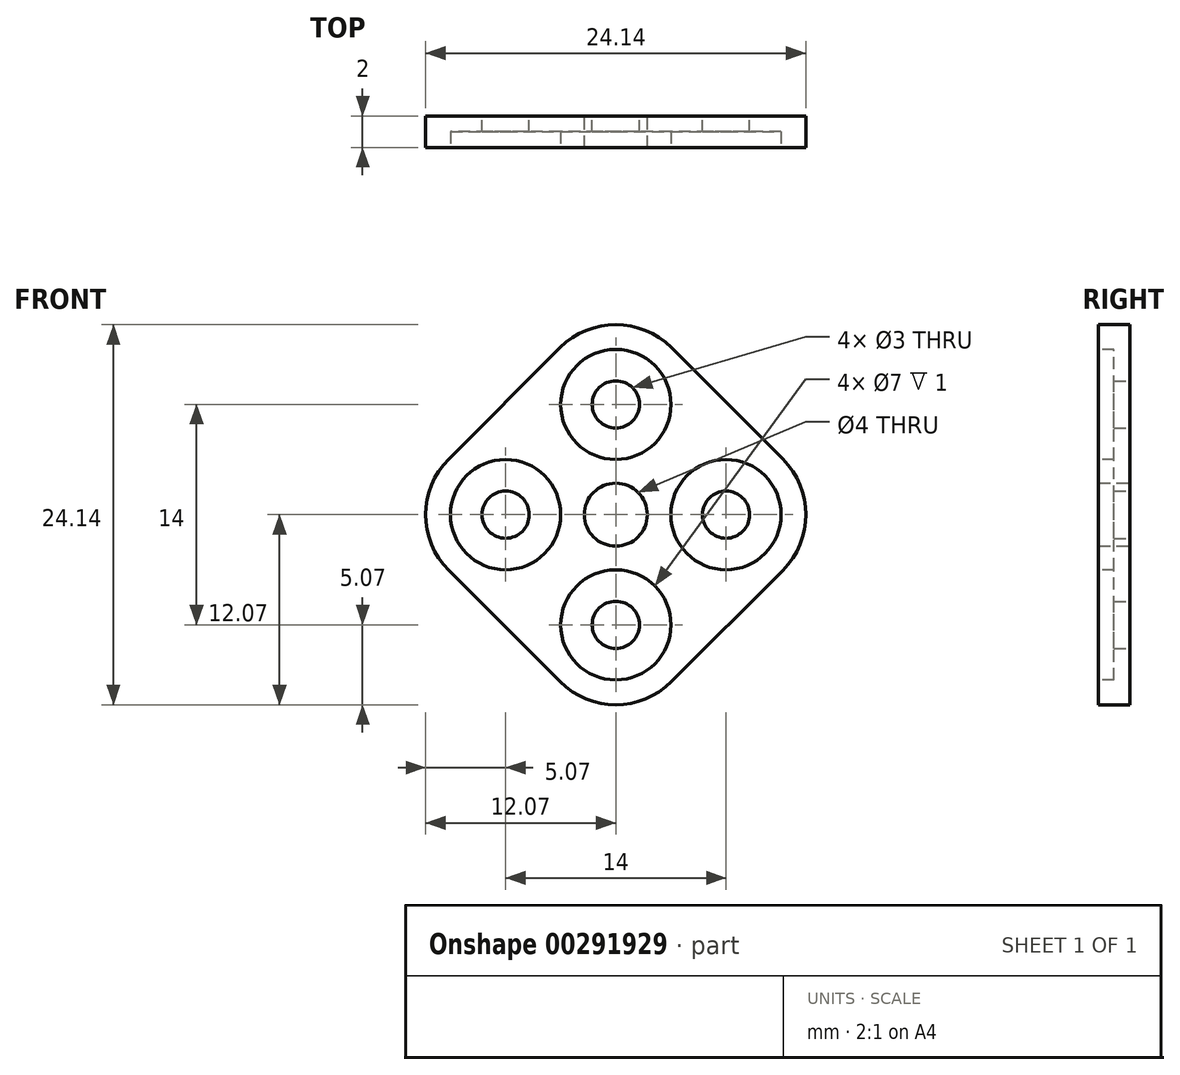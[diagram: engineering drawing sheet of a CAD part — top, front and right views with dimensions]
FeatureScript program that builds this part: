
annotation { "Feature Type Name" : "Feature", "Feature Type Description" : "" }
export const myFeature = defineFeature(function(context is Context, id is Id, definition is map)
    precondition{}
    {
        {
            var Q0;
            Q0=qCreatedBy(makeId("Front.planeOp"),FACE);
            var sketch = newSketch(context, id + "F0", { "sketchPlane" : qUnion([Q0])});
            skPoint(sketch, "E0.middle", {"position": v(0, 0) * mm});
            skCircle(sketch, "E1", {"center": v(0, 0) * mm, "radius": 2 * mm});
            skCircle(sketch, "E2", {"center": v(7, 0) * mm, "radius": 1.5 * mm});
            skCircle(sketch, "E3.1.0", {"center": v(0, 7) * mm, "radius": 1.5 * mm});
            skCircle(sketch, "E3.2.0", {"center": v(-7, 0) * mm, "radius": 1.5 * mm});
            skCircle(sketch, "E3.3.0", {"center": v(0, -7) * mm, "radius": 1.5 * mm});
            skPoint(sketch, "E4.endSnap0", {"position": v(0, -11.8) * mm});
            skLineSegment(sketch, "E5.bottom", {"start": v(-3.54, -10.6) * mm, "end": v(-10.6, -3.54) * mm});
            skLineSegment(sketch, "E5.top", {"start": v(10.6, 3.54) * mm, "end": v(3.54, 10.6) * mm});
            skLineSegment(sketch, "E5.left", {"start": v(3.54, -10.6) * mm, "end": v(10.6, -3.54) * mm});
            skLineSegment(sketch, "E5.right", {"start": v(-10.6, 3.54) * mm, "end": v(-3.54, 10.6) * mm});
            skPoint(sketch, "E6.visualSharp", {"position": v(0, -14.14) * mm});
            skArc(sketch, "E6.filletArc", {"start": v(-3.54, -10.6) * mm, "mid": v(0, -12.07) * mm, "end": v(3.54, -10.6) * mm});
            skPoint(sketch, "E7.visualSharp", {"position": v(-14.14, 0) * mm});
            skArc(sketch, "E7.filletArc", {"start": v(-10.6, 3.54) * mm, "mid": v(-12.07, 0) * mm, "end": v(-10.6, -3.54) * mm});
            skPoint(sketch, "E8.visualSharp", {"position": v(0, 14.14) * mm});
            skArc(sketch, "E8.filletArc", {"start": v(3.54, 10.6) * mm, "mid": v(0, 12.07) * mm, "end": v(-3.54, 10.6) * mm});
            skPoint(sketch, "E9.visualSharp", {"position": v(14.14, 0) * mm});
            skArc(sketch, "E9.filletArc", {"start": v(10.6, -3.54) * mm, "mid": v(12.07, 0) * mm, "end": v(10.6, 3.54) * mm});
            skSolve(sketch);
        }
        {
            var Q0;
            Q0=qSketchRegion(id+"F0",true);
            extrude(context, id + "F1", {"entities" : qUnion([Q0]), "depth" : 2 * mm});
        }
        {
            var Q0;
            Q0=makeQuery(id+"F1.opExtrude","CAP_FACE",FACE,{"disambiguationData":[OSD([sQuery(id+"F0.wireOp",EDGE,"E1"),sQuery(id+"F0.wireOp",EDGE,"E2"),sQuery(id+"F0.wireOp",EDGE,"E3.1.0"),sQuery(id+"F0.wireOp",EDGE,"E3.2.0"),sQuery(id+"F0.wireOp",EDGE,"E3.3.0"),sQuery(id+"F0.wireOp",EDGE,"E5.bottom"),sQuery(id+"F0.wireOp",EDGE,"E5.top"),sQuery(id+"F0.wireOp",EDGE,"E5.left"),sQuery(id+"F0.wireOp",EDGE,"E5.right"),sQuery(id+"F0.wireOp",EDGE,"E6.filletArc"),sQuery(id+"F0.wireOp",EDGE,"E7.filletArc"),sQuery(id+"F0.wireOp",EDGE,"E8.filletArc"),sQuery(id+"F0.wireOp",EDGE,"E9.filletArc")])],"isStart":false});
            var sketch = newSketch(context, id + "F2", { "sketchPlane" : qUnion([Q0])});
            skCircle(sketch, "E10", {"center": v(-7, 0) * mm, "radius": 3.5 * mm});
            skCircle(sketch, "E11.1.0", {"center": v(0, -7) * mm, "radius": 3.5 * mm});
            skCircle(sketch, "E11.2.0", {"center": v(7, 0) * mm, "radius": 3.5 * mm});
            skCircle(sketch, "E11.3.0", {"center": v(0, 7) * mm, "radius": 3.5 * mm});
            skPoint(sketch, "E11.center", {"position": v(0, 0) * mm});
            skSolve(sketch);
        }
        {
            var Q0;
            Q0 = qSketchRegion(id + "F2", true);
            extrude(context, id + "F3", {"entities" : qUnion([Q0]), "operationType" : NewBodyOperationType.REMOVE, "oppositeDirection" : true, "depth" : 1 * mm});
        }
    });
